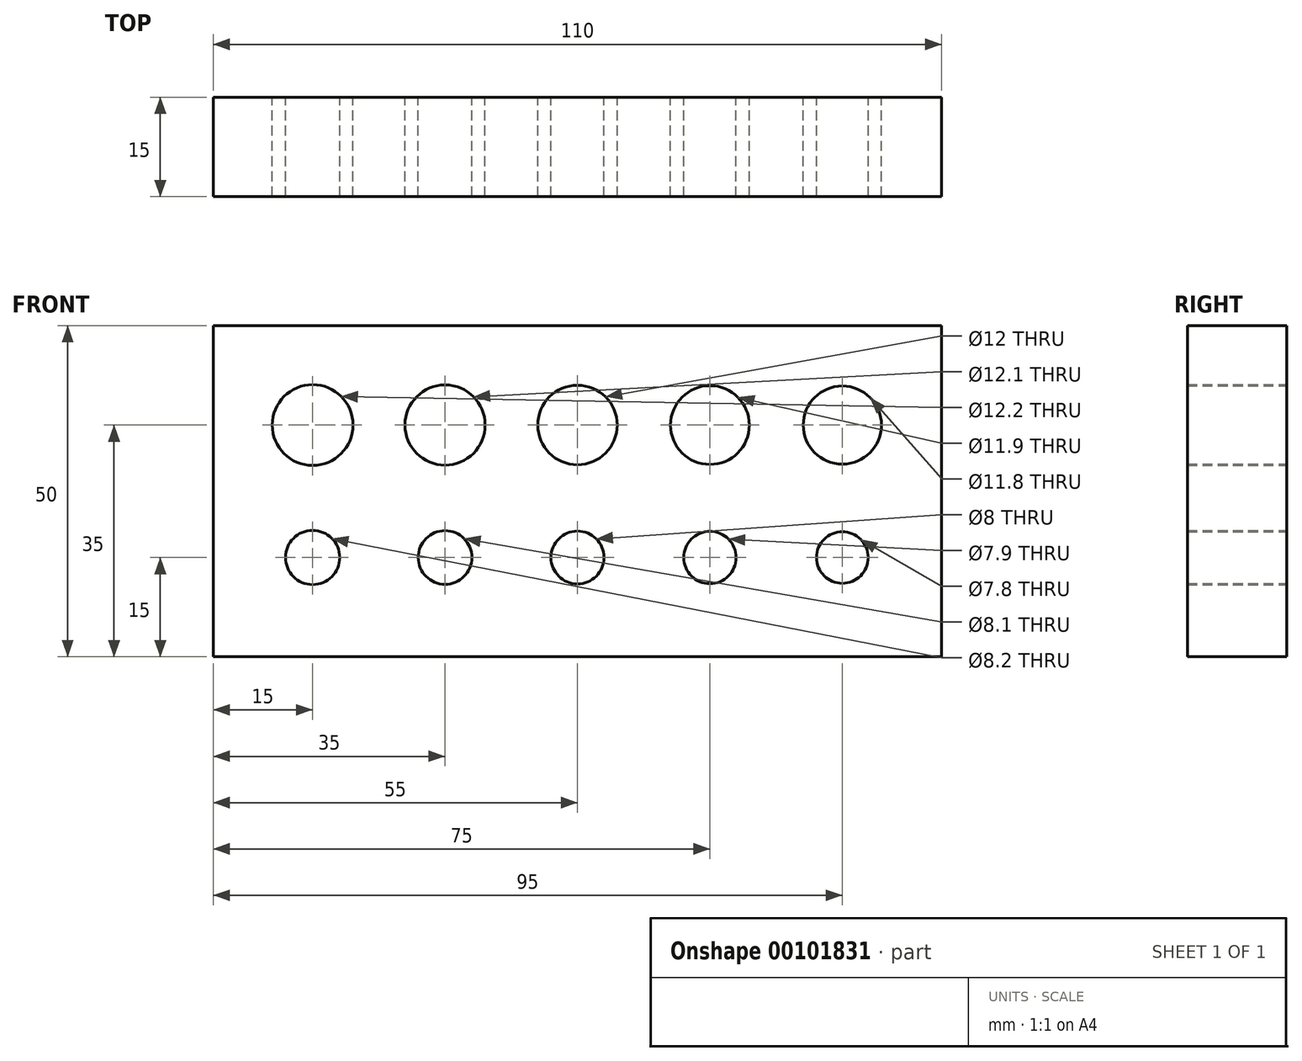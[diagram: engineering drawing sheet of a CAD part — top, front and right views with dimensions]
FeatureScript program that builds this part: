
annotation { "Feature Type Name" : "Feature", "Feature Type Description" : "" }
export const myFeature = defineFeature(function(context is Context, id is Id, definition is map)
    precondition{}
    {
        {
            var Q0;
            Q0=qCreatedBy(makeId("Front.planeOp"),FACE);
            var sketch = newSketch(context, id + "F0", { "sketchPlane" : qUnion([Q0])});
            skLineSegment(sketch, "E0.bottom", {"start": v(-55, 25) * mm, "end": v(55, 25) * mm});
            skLineSegment(sketch, "E0.top", {"start": v(-55, -25) * mm, "end": v(55, -25) * mm});
            skLineSegment(sketch, "E0.left", {"start": v(-55, 25) * mm, "end": v(-55, -25) * mm});
            skLineSegment(sketch, "E0.right", {"start": v(55, 25) * mm, "end": v(55, -25) * mm});
            skPoint(sketch, "E0.middle", {"position": v(0, 0) * mm});
            skCircle(sketch, "E1", {"center": v(0, 10) * mm, "radius": 6 * mm});
            skCircle(sketch, "E2", {"center": v(-20, 10) * mm, "radius": 6.05 * mm});
            skCircle(sketch, "E3", {"center": v(-40, 10) * mm, "radius": 6.1 * mm});
            skCircle(sketch, "E4", {"center": v(20, 10) * mm, "radius": 5.95 * mm});
            skCircle(sketch, "E5", {"center": v(40, 10) * mm, "radius": 5.9 * mm});
            skCircle(sketch, "E6", {"center": v(0, -10) * mm, "radius": 4 * mm});
            skCircle(sketch, "E7", {"center": v(20, -10) * mm, "radius": 3.95 * mm});
            skCircle(sketch, "E8", {"center": v(40, -10) * mm, "radius": 3.9 * mm});
            skCircle(sketch, "E9", {"center": v(-20, -10) * mm, "radius": 4.05 * mm});
            skCircle(sketch, "E10", {"center": v(-40, -10) * mm, "radius": 4.1 * mm});
            skSolve(sketch);
        }
        {
            var Q0;
            Q0=makeQuery(id+"F0.imprint","IMPRINT",FACE,{"disambiguationData":[TD([[makeQuery(id+"F0.imprint","IMPRINT",EDGE,{"derivedFrom":sQuery(id+"F0.wireOp",EDGE,"E0.bottom")}),-1.0]])]});
            extrude(context, id + "F1", {"entities" : qUnion([Q0]), "depth" : 15 * mm});
        }
    });
